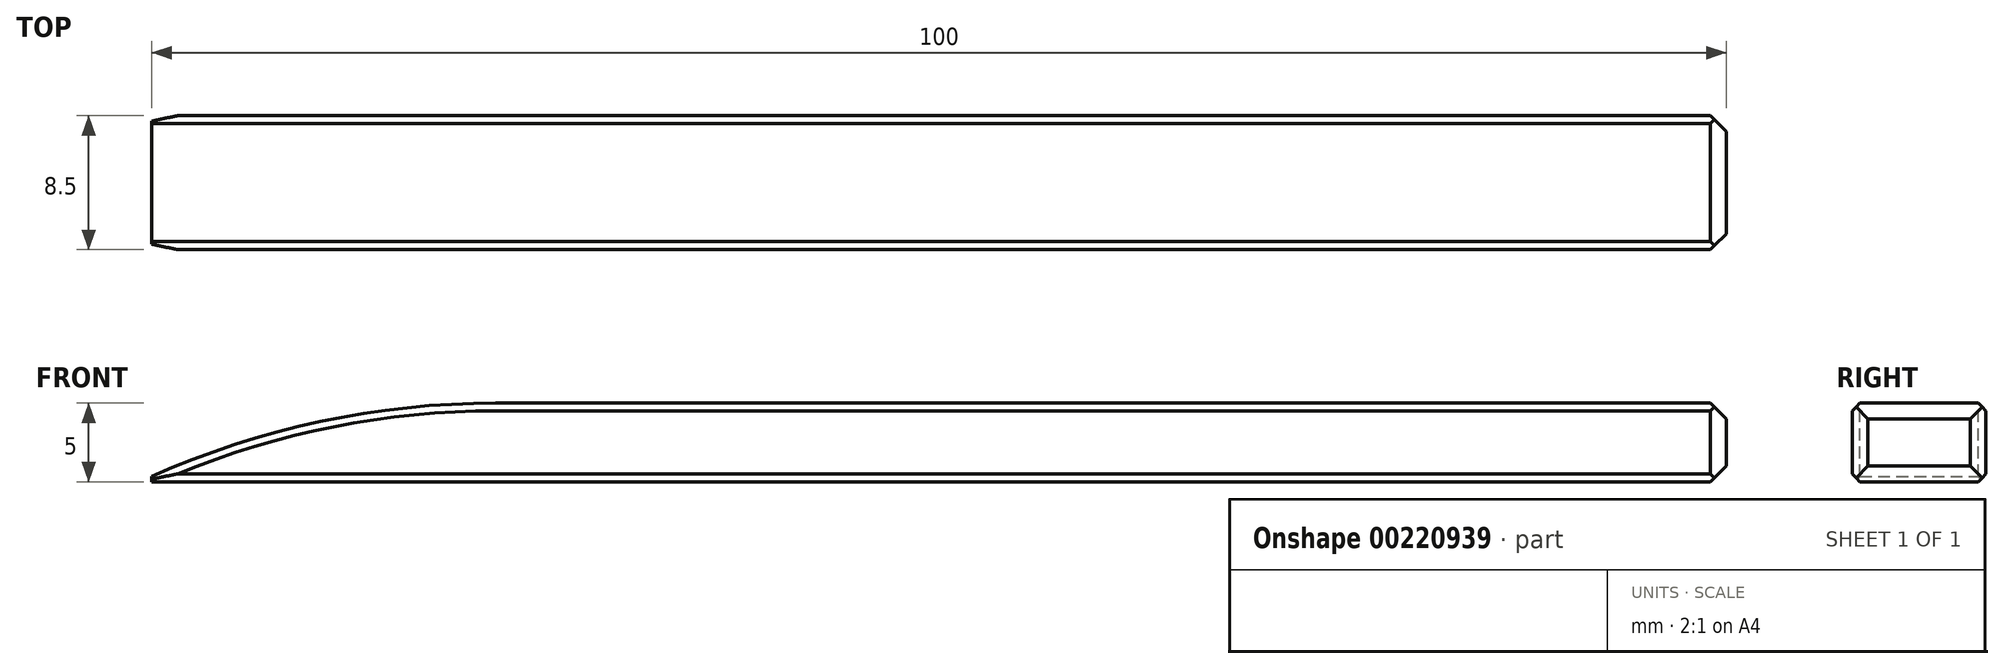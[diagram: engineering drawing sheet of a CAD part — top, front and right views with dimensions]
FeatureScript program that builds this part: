
annotation { "Feature Type Name" : "Feature", "Feature Type Description" : "" }
export const myFeature = defineFeature(function(context is Context, id is Id, definition is map)
    precondition{}
    {
        {
            var Q0;
            Q0=qCreatedBy(makeId("Top.planeOp"),FACE);
            var sketch = newSketch(context, id + "F0", { "sketchPlane" : qUnion([Q0])});
            skLineSegment(sketch, "E0.bottom", {"start": v(-50, 4.25) * mm, "end": v(50, 4.25) * mm});
            skLineSegment(sketch, "E0.top", {"start": v(-50, -4.25) * mm, "end": v(50, -4.25) * mm});
            skLineSegment(sketch, "E0.left", {"start": v(-50, 4.25) * mm, "end": v(-50, -4.25) * mm});
            skLineSegment(sketch, "E0.right", {"start": v(50, 4.25) * mm, "end": v(50, -4.25) * mm});
            skLineSegment(sketch, "E1", {"start": v(-50, -4.25) * mm, "end": v(50, 4.25) * mm, "construction": true});
            skLineSegment(sketch, "E2", {"start": v(0, -4.25) * mm, "end": v(0, 4.25) * mm});
            skSolve(sketch);
        }
        {
            var Q0;
            Q0=makeQuery(id+"F0.imprint","IMPRINT",FACE,{"disambiguationData":[TD([[makeQuery(id+"F0.imprint","IMPRINT",EDGE,{"derivedFrom":sQuery(id+"F0.wireOp",EDGE,"E0.bottom")}),-1.0]])]});
            extrude(context, id + "F1", {"entities" : qUnion([Q0]), "depth" : 5 * mm});
        }
        {
            var Q0;
            Q0=makeQuery(id+"F1.opExtrude","CAP_EDGE",EDGE,{"disambiguationData":[OSD([sQuery(id+"F0.wireOp",EDGE,"E0.left")])],"isStart":false});
            chamfer(context, id + "F2", {"entities" : qUnion([Q0]), "chamferType" : ChamferType.OFFSET_ANGLE, "width" : 10 * mm, "oppositeDirection" : false, "angle" : 25 * degree});
        }
        {
            var Q0;
            {var subQ0=sQuery(id+"F0.wireOp",EDGE,"E0.left");Q0=makeQuery(id+"F2.opChamfer","BLEND_EDGE",EDGE,{"blendedFrom":[makeQuery(id+"F1.opExtrude","CAP_EDGE",EDGE,{"disambiguationData":[OSD([subQ0])],"isStart":false}),makeQuery(id+"F1.opExtrude","CAP_FACE",FACE,{"disambiguationData":[OSD([sQuery(id+"F0.wireOp",EDGE,"E0.bottom"),sQuery(id+"F0.wireOp",EDGE,"E0.top"),subQ0,sQuery(id+"F0.wireOp",EDGE,"E0.right")])],"isStart":false})],"blendedInto":[makeQuery(id+"F1.opExtrude","CAP_FACE",FACE,{"disambiguationData":[OSD([sQuery(id+"F0.wireOp",EDGE,"E0.bottom"),sQuery(id+"F0.wireOp",EDGE,"E0.top"),subQ0,sQuery(id+"F0.wireOp",EDGE,"E0.right")])],"isStart":false})]});}
            fillet(context, id + "F3", {"entities" : qUnion([Q0]), "radius" : 53.54 * mm, "allowEdgeOverflow" : false});
        }
        {
            var Q0;
            Q0=makeQuery(id+"F1.opExtrude","CAP_EDGE",EDGE,{"disambiguationData":[OSD([sQuery(id+"F0.wireOp",EDGE,"E0.bottom")])],"isStart":false});
            var Q1;
            Q1=makeQuery(id+"F1.opExtrude","CAP_EDGE",EDGE,{"disambiguationData":[OSD([sQuery(id+"F0.wireOp",EDGE,"E0.top")])],"isStart":false});
            var Q2;
            Q2=makeQuery(id+"F1.opExtrude","CAP_EDGE",EDGE,{"disambiguationData":[OSD([sQuery(id+"F0.wireOp",EDGE,"E0.top")])],"isStart":true});
            var Q3;
            Q3=makeQuery(id+"F1.opExtrude","CAP_EDGE",EDGE,{"disambiguationData":[OSD([sQuery(id+"F0.wireOp",EDGE,"E0.bottom")])],"isStart":true});
            chamfer(context, id + "F4", {"entities" : qUnion([Q0, Q1, Q2, Q3]), "width" : 0.5 * mm, "tangentPropagation" : true});
        }
        {
            var Q0;
            Q0=makeQuery(id+"F1.opExtrude","CAP_EDGE",EDGE,{"disambiguationData":[OSD([sQuery(id+"F0.wireOp",EDGE,"E0.right")])],"isStart":true});
            var Q1;
            Q1=makeQuery(id+"F1.opExtrude","SWEPT_EDGE",EDGE,{"disambiguationData":[OSD([sQuery(id+"F0.wireOp",EDGE,"E0.top"),sQuery(id+"F0.wireOp",EDGE,"E0.right")])]});
            var Q2;
            Q2=makeQuery(id+"F1.opExtrude","CAP_EDGE",EDGE,{"disambiguationData":[OSD([sQuery(id+"F0.wireOp",EDGE,"E0.right")])],"isStart":false});
            var Q3;
            Q3=makeQuery(id+"F1.opExtrude","SWEPT_EDGE",EDGE,{"disambiguationData":[OSD([sQuery(id+"F0.wireOp",EDGE,"E0.bottom"),sQuery(id+"F0.wireOp",EDGE,"E0.right")])]});
            chamfer(context, id + "F5", {"entities" : qUnion([Q0, Q1, Q2, Q3]), "width" : 1 * mm, "tangentPropagation" : true});
        }
    });
